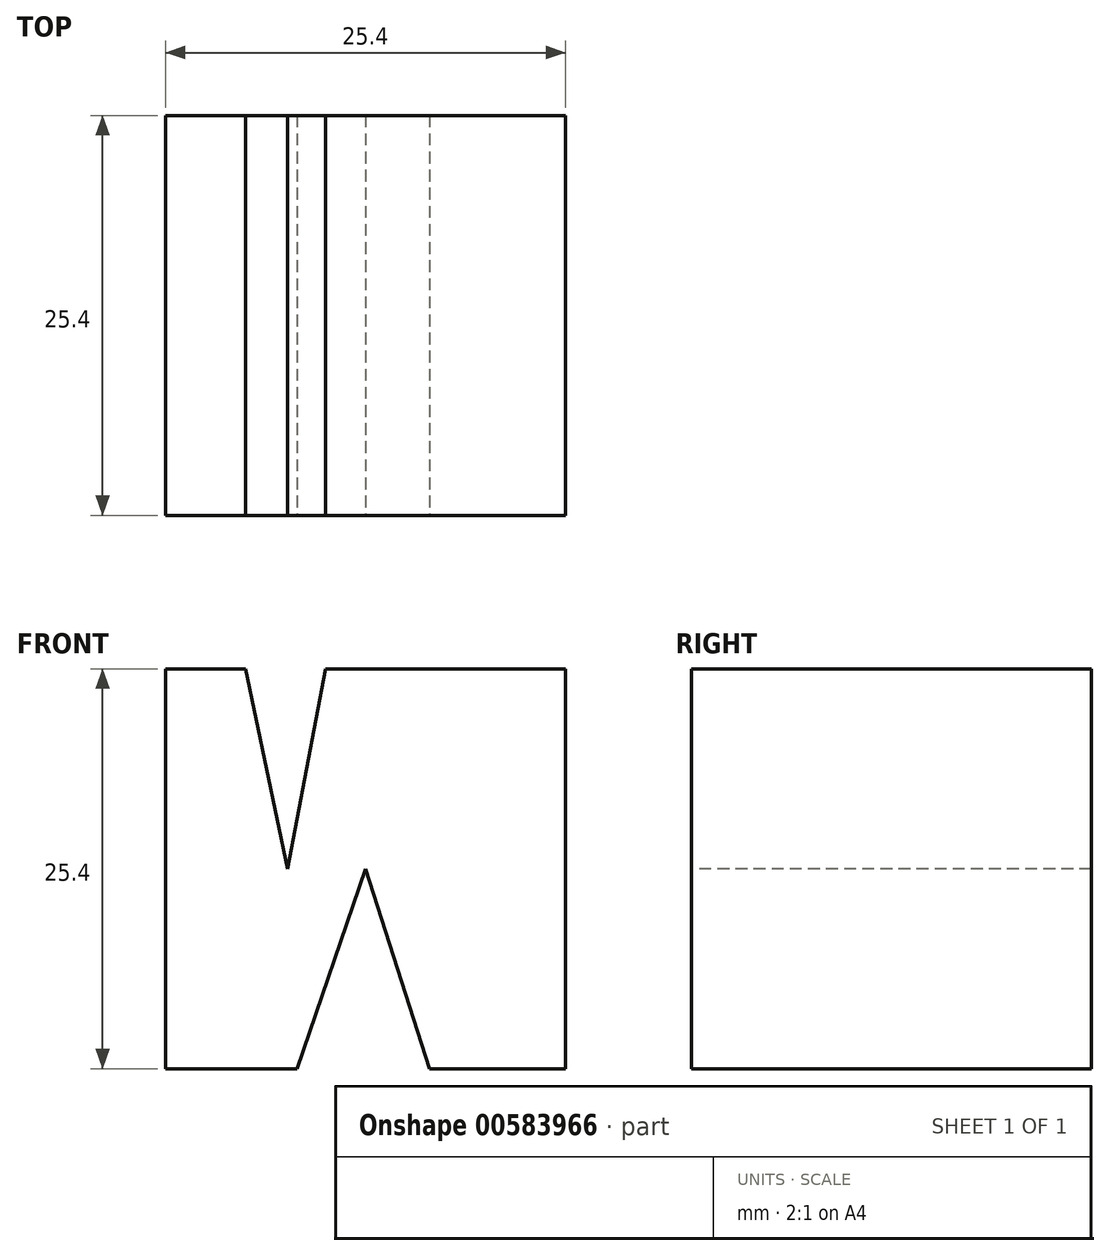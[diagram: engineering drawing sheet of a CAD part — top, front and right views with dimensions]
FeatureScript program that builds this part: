
annotation { "Feature Type Name" : "Feature", "Feature Type Description" : "" }
export const myFeature = defineFeature(function(context is Context, id is Id, definition is map)
    precondition{}
    {
        {
            var Q0;
            Q0=qCreatedBy(makeId("Top.planeOp"),FACE);
            var sketch = newSketch(context, id + "F0", { "sketchPlane" : qUnion([Q0])});
            skLineSegment(sketch, "E0.bottom", {"start": v(12.7, 12.7) * mm, "end": v(-12.7, 12.7) * mm});
            skLineSegment(sketch, "E0.top", {"start": v(12.7, -12.7) * mm, "end": v(-12.7, -12.7) * mm});
            skLineSegment(sketch, "E0.left", {"start": v(12.7, 12.7) * mm, "end": v(12.7, -12.7) * mm});
            skLineSegment(sketch, "E0.right", {"start": v(-12.7, 12.7) * mm, "end": v(-12.7, -12.7) * mm});
            skPoint(sketch, "E0.middle", {"position": v(0, 0) * mm});
            skSolve(sketch);
        }
        {
            var Q0;
            Q0=makeQuery(id+"F0.imprint","IMPRINT",FACE,{"disambiguationData":[TD([[makeQuery(id+"F0.imprint","IMPRINT",EDGE,{"derivedFrom":sQuery(id+"F0.wireOp",EDGE,"E0.bottom")}),1.0]])]});
            extrude(context, id + "F1", {"entities" : qUnion([Q0]), "oppositeDirection" : true, "depth" : 25.4 * mm, "offsetDistance" : 25.4 * mm});
        }
        {
            var Q0;
            Q0=makeQuery(id+"F1.opExtrude","SWEPT_FACE",FACE,{"disambiguationData":[OSD([sQuery(id+"F0.wireOp",EDGE,"E0.top")])]});
            var sketch = newSketch(context, id + "F2", { "sketchPlane" : qUnion([Q0])});
            skLineSegment(sketch, "E1", {"start": v(-4.36, -25.4) * mm, "end": v(0, -12.7) * mm});
            skLineSegment(sketch, "E2", {"start": v(0, -12.7) * mm, "end": v(4.06, -25.4) * mm});
            skSolve(sketch);
        }
        {
            var Q0;
            {var subQ0=sQuery(id+"F2.wireOp",EDGE,"E1");Q0=makeQuery(id+"F2.imprint","IMPRINT",FACE,{"disambiguationData":[TD([[makeQuery(id+"F2.imprint","IMPRINT",EDGE,{"derivedFrom":subQ0}),-1.0]])]});}
            extrude(context, id + "F3", {"entities" : qUnion([Q0]), "operationType" : NewBodyOperationType.REMOVE, "oppositeDirection" : true, "depth" : 25.4 * mm, "offsetDistance" : 25.4 * mm});
        }
        {
            var Q0;
            Q0=makeQuery(id+"F1.opExtrude","SWEPT_FACE",FACE,{"disambiguationData":[OSD([sQuery(id+"F0.wireOp",EDGE,"E0.top")])]});
            var sketch = newSketch(context, id + "F4", { "sketchPlane" : qUnion([Q0])});
            skLineSegment(sketch, "E3", {"start": v(-7.62, 0) * mm, "end": v(-4.96, -12.7) * mm});
            skLineSegment(sketch, "E4", {"start": v(-2.54, 0) * mm, "end": v(-4.96, -12.7) * mm});
            skSolve(sketch);
        }
        {
            var Q0;
            {var subQ0=sQuery(id+"F4.wireOp",EDGE,"E3");Q0=makeQuery(id+"F4.imprint","IMPRINT",FACE,{"disambiguationData":[TD([[makeQuery(id+"F4.imprint","IMPRINT",EDGE,{"derivedFrom":subQ0}),1.0]])]});}
            extrude(context, id + "F5", {"entities" : qUnion([Q0]), "operationType" : NewBodyOperationType.REMOVE, "oppositeDirection" : true, "depth" : 25.4 * mm, "offsetDistance" : 25.4 * mm});
        }
    });
